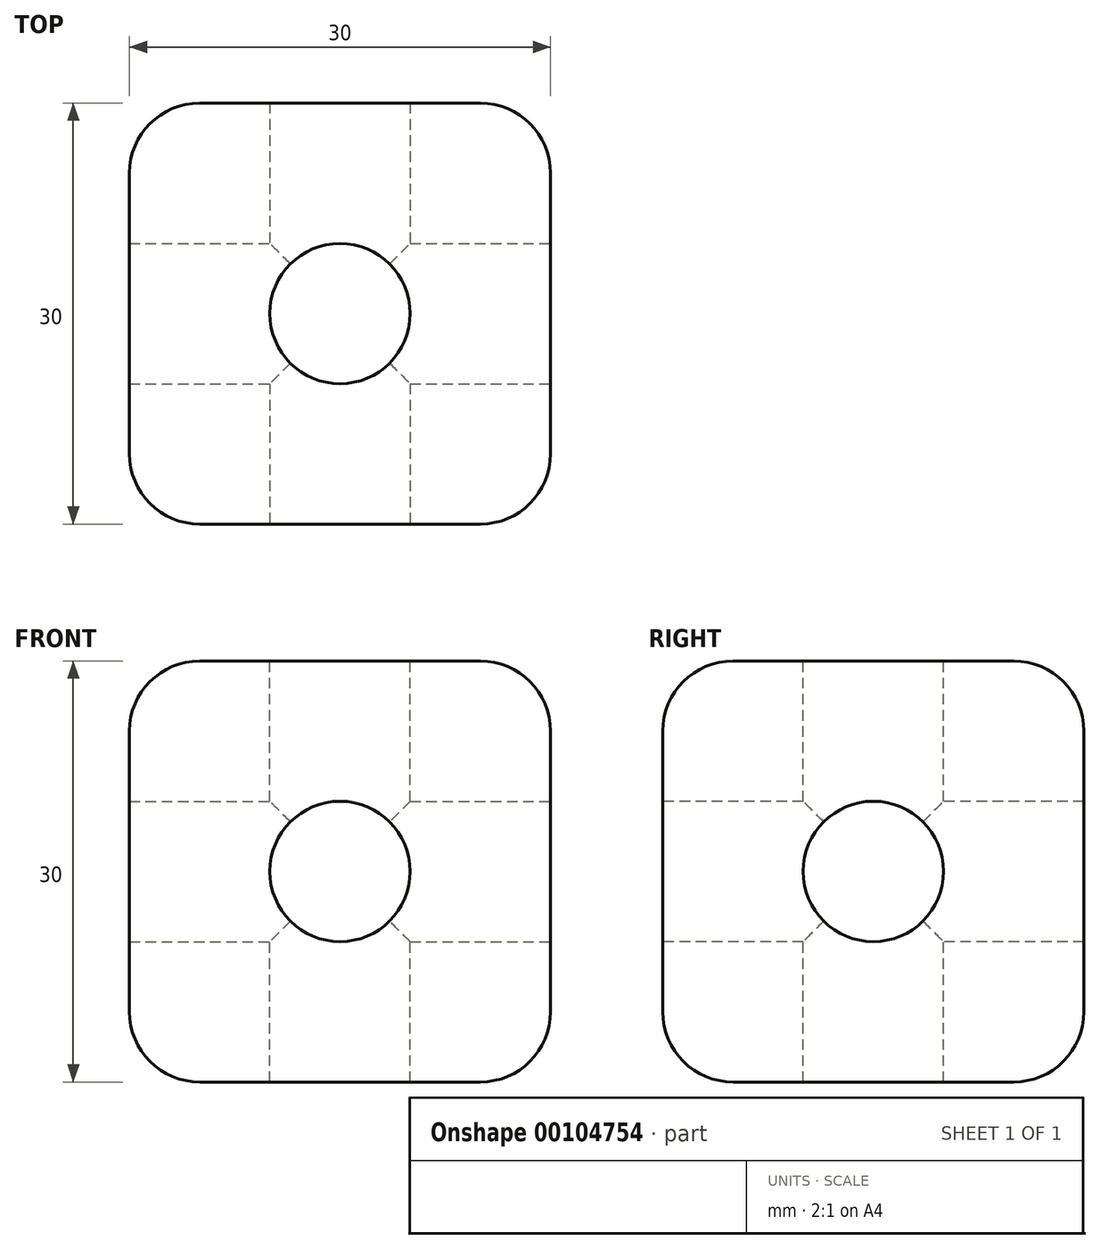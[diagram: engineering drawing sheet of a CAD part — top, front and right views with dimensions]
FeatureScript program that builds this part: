
annotation { "Feature Type Name" : "Feature", "Feature Type Description" : "" }
export const myFeature = defineFeature(function(context is Context, id is Id, definition is map)
    precondition{}
    {
        {
            var Q0;
            Q0=qCreatedBy(makeId("Top.planeOp"),FACE);
            var sketch = newSketch(context, id + "F0", { "sketchPlane" : qUnion([Q0])});
            skLineSegment(sketch, "E0.bottom", {"start": v(15, 15) * mm, "end": v(-15, 15) * mm});
            skLineSegment(sketch, "E0.top", {"start": v(15, -15) * mm, "end": v(-15, -15) * mm});
            skLineSegment(sketch, "E0.left", {"start": v(15, 15) * mm, "end": v(15, -15) * mm});
            skLineSegment(sketch, "E0.right", {"start": v(-15, 15) * mm, "end": v(-15, -15) * mm});
            skPoint(sketch, "E0.middle", {"position": v(0, 0) * mm});
            skSolve(sketch);
        }
        {
            var Q0;
            Q0=makeQuery(id+"F0.imprint","IMPRINT",FACE,{"disambiguationData":[TD([[makeQuery(id+"F0.imprint","IMPRINT",EDGE,{"derivedFrom":sQuery(id+"F0.wireOp",EDGE,"E0.bottom")}),1.0]])]});
            extrude(context, id + "F1", {"entities" : qUnion([Q0]), "depth" : 30 * mm, "symmetric" : true});
        }
        {
            var Q0;
            Q0=makeQuery(id+"F1.opExtrude","CAP_FACE",FACE,{"disambiguationData":[OSD([sQuery(id+"F0.wireOp",EDGE,"E0.bottom"),sQuery(id+"F0.wireOp",EDGE,"E0.top"),sQuery(id+"F0.wireOp",EDGE,"E0.left"),sQuery(id+"F0.wireOp",EDGE,"E0.right")])],"isStart":false});
            var sketch = newSketch(context, id + "F2", { "sketchPlane" : qUnion([Q0])});
            skCircle(sketch, "E1", {"center": v(0, 0) * mm, "radius": 5 * mm});
            skSolve(sketch);
        }
        {
            var Q0;
            Q0=makeQuery(id+"F2.imprint","IMPRINT",FACE,{"disambiguationData":[TD([[makeQuery(id+"F2.imprint","IMPRINT",EDGE,{"derivedFrom":sQuery(id+"F2.wireOp",EDGE,"E1")}),1.0]])]});
            extrude(context, id + "F3", {"entities" : qUnion([Q0]), "operationType" : NewBodyOperationType.REMOVE, "endBound" : BoundingType.THROUGH_ALL, "oppositeDirection" : true, "depth" : 25 * mm});
        }
        {
            var Q0;
            Q0=makeQuery(id+"F1.opExtrude","SWEPT_FACE",FACE,{"disambiguationData":[OSD([sQuery(id+"F0.wireOp",EDGE,"E0.left")])]});
            var sketch = newSketch(context, id + "F4", { "sketchPlane" : qUnion([Q0])});
            skCircle(sketch, "E2", {"center": v(0, 0) * mm, "radius": 5 * mm});
            skSolve(sketch);
        }
        {
            var Q0;
            Q0=makeQuery(id+"F4.imprint","IMPRINT",FACE,{"disambiguationData":[TD([[makeQuery(id+"F4.imprint","IMPRINT",EDGE,{"derivedFrom":sQuery(id+"F4.wireOp",EDGE,"E2")}),1.0]])]});
            extrude(context, id + "F5", {"entities" : qUnion([Q0]), "operationType" : NewBodyOperationType.REMOVE, "endBound" : BoundingType.THROUGH_ALL, "oppositeDirection" : true, "depth" : 25 * mm});
        }
        {
            var Q0;
            Q0=makeQuery(id+"F1.opExtrude","SWEPT_FACE",FACE,{"disambiguationData":[OSD([sQuery(id+"F0.wireOp",EDGE,"E0.top")])]});
            var sketch = newSketch(context, id + "F6", { "sketchPlane" : qUnion([Q0])});
            skCircle(sketch, "E3", {"center": v(0, 0) * mm, "radius": 5 * mm});
            skSolve(sketch);
        }
        {
            var Q0;
            Q0=makeQuery(id+"F6.imprint","IMPRINT",FACE,{"disambiguationData":[TD([[makeQuery(id+"F6.imprint","IMPRINT",EDGE,{"derivedFrom":sQuery(id+"F6.wireOp",EDGE,"E3")}),1.0]])]});
            extrude(context, id + "F7", {"entities" : qUnion([Q0]), "operationType" : NewBodyOperationType.REMOVE, "endBound" : BoundingType.THROUGH_ALL, "oppositeDirection" : true, "depth" : 25 * mm});
        }
        {
            var Q0;
            Q0=makeQuery(id+"F1.opExtrude","CAP_EDGE",EDGE,{"disambiguationData":[OSD([sQuery(id+"F0.wireOp",EDGE,"E0.left")])],"isStart":false});
            var Q1;
            Q1=makeQuery(id+"F1.opExtrude","CAP_EDGE",EDGE,{"disambiguationData":[OSD([sQuery(id+"F0.wireOp",EDGE,"E0.bottom")])],"isStart":false});
            var Q2;
            Q2=makeQuery(id+"F1.opExtrude","CAP_EDGE",EDGE,{"disambiguationData":[OSD([sQuery(id+"F0.wireOp",EDGE,"E0.top")])],"isStart":false});
            var Q3;
            Q3=makeQuery(id+"F1.opExtrude","CAP_EDGE",EDGE,{"disambiguationData":[OSD([sQuery(id+"F0.wireOp",EDGE,"E0.right")])],"isStart":false});
            var Q4;
            Q4=makeQuery(id+"F1.opExtrude","SWEPT_EDGE",EDGE,{"disambiguationData":[OSD([sQuery(id+"F0.wireOp",EDGE,"E0.bottom"),sQuery(id+"F0.wireOp",EDGE,"E0.right")])]});
            var Q5;
            Q5=makeQuery(id+"F1.opExtrude","SWEPT_EDGE",EDGE,{"disambiguationData":[OSD([sQuery(id+"F0.wireOp",EDGE,"E0.top"),sQuery(id+"F0.wireOp",EDGE,"E0.left")])]});
            var Q6;
            Q6=makeQuery(id+"F1.opExtrude","CAP_EDGE",EDGE,{"disambiguationData":[OSD([sQuery(id+"F0.wireOp",EDGE,"E0.top")])],"isStart":true});
            var Q7;
            Q7=makeQuery(id+"F1.opExtrude","CAP_EDGE",EDGE,{"disambiguationData":[OSD([sQuery(id+"F0.wireOp",EDGE,"E0.right")])],"isStart":true});
            var Q8;
            Q8=makeQuery(id+"F1.opExtrude","SWEPT_EDGE",EDGE,{"disambiguationData":[OSD([sQuery(id+"F0.wireOp",EDGE,"E0.bottom"),sQuery(id+"F0.wireOp",EDGE,"E0.left")])]});
            var Q9;
            Q9=makeQuery(id+"F1.opExtrude","CAP_EDGE",EDGE,{"disambiguationData":[OSD([sQuery(id+"F0.wireOp",EDGE,"E0.left")])],"isStart":true});
            var Q10;
            Q10=makeQuery(id+"F1.opExtrude","SWEPT_EDGE",EDGE,{"disambiguationData":[OSD([sQuery(id+"F0.wireOp",EDGE,"E0.top"),sQuery(id+"F0.wireOp",EDGE,"E0.right")])]});
            fillet(context, id + "F8", {"entities" : qUnion([Q0, Q1, Q2, Q3, Q4, Q5, Q6, Q7, Q8, Q9, Q10]), "radius" : 5 * mm, "tangentPropagation" : true, "allowEdgeOverflow" : false});
        }
        {
            var Q0;
            Q0=makeQuery(id+"F1.opExtrude","CAP_EDGE",EDGE,{"disambiguationData":[OSD([sQuery(id+"F0.wireOp",EDGE,"E0.bottom")])],"isStart":true});
            fillet(context, id + "F9", {"entities" : qUnion([Q0]), "radius" : 5 * mm, "tangentPropagation" : true, "allowEdgeOverflow" : false});
        }
    });
